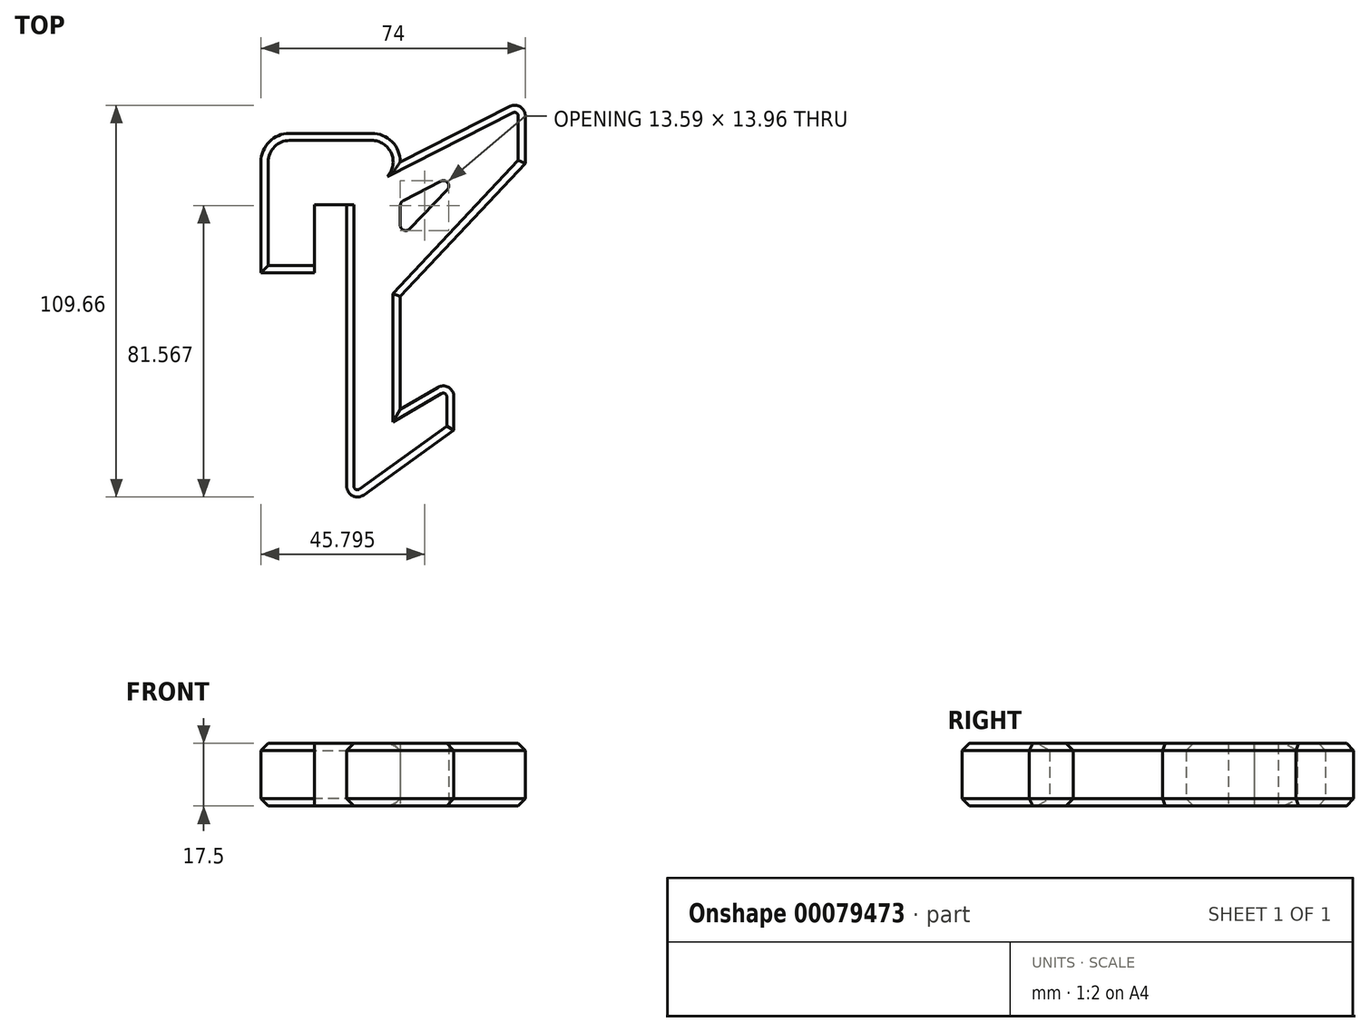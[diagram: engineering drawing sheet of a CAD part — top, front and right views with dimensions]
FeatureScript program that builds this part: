
annotation { "Feature Type Name" : "Feature", "Feature Type Description" : "" }
export const myFeature = defineFeature(function(context is Context, id is Id, definition is map)
    precondition{}
    {
        {
            var Q0;
            Q0=qCreatedBy(makeId("Top.planeOp"),FACE);
            var sketch = newSketch(context, id + "F0", { "sketchPlane" : qUnion([Q0])});
            skLineSegment(sketch, "E0", {"start": v(0, 0) * mm, "end": v(0, -74.06) * mm});
            skLineSegment(sketch, "E1", {"start": v(-9, 0) * mm, "end": v(-9, -19) * mm, "construction": true});
            skLineSegment(sketch, "E2", {"start": v(15, -25.65) * mm, "end": v(50, 11.63) * mm});
            skLineSegment(sketch, "E3", {"start": v(50, 11.63) * mm, "end": v(50, 24.87) * mm});
            skLineSegment(sketch, "E4", {"start": v(45.64, 27.54) * mm, "end": v(15, 12) * mm});
            skLineSegment(sketch, "E5", {"start": v(15, -25.65) * mm, "end": v(15, -57.31) * mm});
            skLineSegment(sketch, "E6", {"start": v(15, -57.31) * mm, "end": v(25.47, -51.12) * mm});
            skLineSegment(sketch, "E7", {"start": v(30, -53.7) * mm, "end": v(30, -63.05) * mm});
            skLineSegment(sketch, "E8", {"start": v(30, -63.05) * mm, "end": v(4.75, -81.23) * mm});
            skLineSegment(sketch, "E9", {"start": v(0, -78.8) * mm, "end": v(0, 0) * mm});
            skLineSegment(sketch, "E10", {"start": v(-9, 0) * mm, "end": v(-9, -19) * mm});
            skPoint(sketch, "E11.visualSharp", {"position": v(50, 29.75) * mm});
            skArc(sketch, "E11.filletArc", {"start": v(50, 24.87) * mm, "mid": v(48.57, 27.43) * mm, "end": v(45.64, 27.54) * mm});
            skPoint(sketch, "E12.visualSharp", {"position": v(30, -48.45) * mm});
            skArc(sketch, "E12.filletArc", {"start": v(30, -53.7) * mm, "mid": v(28.49, -51.1) * mm, "end": v(25.47, -51.12) * mm});
            skPoint(sketch, "E13.visualSharp", {"position": v(0, -84.65) * mm});
            skArc(sketch, "E13.filletArc", {"start": v(0, -78.8) * mm, "mid": v(1.63, -81.46) * mm, "end": v(4.75, -81.23) * mm});
            skLineSegment(sketch, "E14", {"start": v(-24, -19) * mm, "end": v(-24, 12) * mm});
            skLineSegment(sketch, "E15", {"start": v(-16, 20) * mm, "end": v(7, 20) * mm});
            skLineSegment(sketch, "E16", {"start": v(15, 12) * mm, "end": v(15, 12) * mm});
            skPoint(sketch, "E17.visualSharp", {"position": v(15, 20) * mm});
            skArc(sketch, "E17.filletArc", {"start": v(15, 12) * mm, "mid": v(12.66, 17.66) * mm, "end": v(7, 20) * mm});
            skPoint(sketch, "E18.visualSharp", {"position": v(-24, 20) * mm});
            skArc(sketch, "E18.filletArc", {"start": v(-16, 20) * mm, "mid": v(-21.66, 17.66) * mm, "end": v(-24, 12) * mm});
            skLineSegment(sketch, "E19", {"start": v(-24, -19) * mm, "end": v(-9, -19) * mm});
            skLineSegment(sketch, "E20", {"start": v(-9, 0) * mm, "end": v(0, 0) * mm});
            skLineSegment(sketch, "E21", {"start": v(15, -0.24) * mm, "end": v(15, -5.7) * mm});
            skLineSegment(sketch, "E22", {"start": v(17.58, -6.75) * mm, "end": v(28.17, 4.23) * mm});
            skLineSegment(sketch, "E23", {"start": v(26.4, 6.6) * mm, "end": v(15.8, 1.1) * mm});
            skPoint(sketch, "E24.visualSharp", {"position": v(15, 0.67) * mm});
            skArc(sketch, "E24.filletArc", {"start": v(15.8, 1.1) * mm, "mid": v(15.22, 0.54) * mm, "end": v(15, -0.24) * mm});
            skPoint(sketch, "E25.visualSharp", {"position": v(34.55, 10.84) * mm});
            skArc(sketch, "E25.filletArc", {"start": v(28.17, 4.23) * mm, "mid": v(28.3, 6.17) * mm, "end": v(26.4, 6.6) * mm});
            skPoint(sketch, "E26.visualSharp", {"position": v(15, -9.42) * mm});
            skArc(sketch, "E26.filletArc", {"start": v(15, -5.7) * mm, "mid": v(15.94, -7.1) * mm, "end": v(17.58, -6.75) * mm});
            skSolve(sketch);
        }
        {
            var Q0;
            Q0=makeQuery(id+"F0.imprint","IMPRINT",FACE,{"disambiguationData":[TD([[makeQuery(id+"F0.imprint","IMPRINT",EDGE,{"derivedFrom":sQuery(id+"F0.wireOp",EDGE,"E2")}),1.0]])]});
            extrude(context, id + "F1", {"entities" : qUnion([Q0]), "depth" : 17.5 * mm, "offsetDistance" : 25 * mm});
        }
        {
            var Q0;
            Q0=makeQuery(id+"F1.opExtrude","CAP_EDGE",EDGE,{"disambiguationData":[OSD([sQuery(id+"F0.wireOp",EDGE,"E4")])],"isStart":false});
            var Q1;
            Q1=makeQuery(id+"F1.opExtrude","CAP_EDGE",EDGE,{"disambiguationData":[OSD([sQuery(id+"F0.wireOp",EDGE,"E2")])],"isStart":false});
            var Q2;
            Q2=makeQuery(id+"F1.opExtrude","CAP_EDGE",EDGE,{"disambiguationData":[OSD([sQuery(id+"F0.wireOp",EDGE,"E3")])],"isStart":false});
            var Q3;
            Q3=makeQuery(id+"F1.opExtrude","CAP_EDGE",EDGE,{"disambiguationData":[OSD([sQuery(id+"F0.wireOp",EDGE,"E5")])],"isStart":false});
            var Q4;
            Q4=makeQuery(id+"F1.opExtrude","CAP_EDGE",EDGE,{"disambiguationData":[OSD([sQuery(id+"F0.wireOp",EDGE,"E6")])],"isStart":false});
            var Q5;
            Q5=makeQuery(id+"F1.opExtrude","CAP_EDGE",EDGE,{"disambiguationData":[OSD([sQuery(id+"F0.wireOp",EDGE,"E8")])],"isStart":false});
            var Q6;
            Q6=makeQuery(id+"F1.opExtrude","CAP_EDGE",EDGE,{"disambiguationData":[OSD([sQuery(id+"F0.wireOp",EDGE,"E15")])],"isStart":false});
            var Q7;
            Q7=makeQuery(id+"F1.opExtrude","CAP_EDGE",EDGE,{"disambiguationData":[OSD([sQuery(id+"F0.wireOp",EDGE,"E17.filletArc")])],"isStart":false});
            var Q8;
            Q8=makeQuery(id+"F1.opExtrude","CAP_EDGE",EDGE,{"disambiguationData":[OSD([sQuery(id+"F0.wireOp",EDGE,"E19")])],"isStart":false});
            var Q9;
            Q9=makeQuery(id+"F1.opExtrude","CAP_EDGE",EDGE,{"disambiguationData":[OSD([sQuery(id+"F0.wireOp",EDGE,"E9")])],"isStart":false});
            var Q10;
            Q10=makeQuery(id+"F1.opExtrude","CAP_EDGE",EDGE,{"disambiguationData":[OSD([sQuery(id+"F0.wireOp",EDGE,"E7")])],"isStart":true});
            var Q11;
            Q11=makeQuery(id+"F1.opExtrude","CAP_EDGE",EDGE,{"disambiguationData":[OSD([sQuery(id+"F0.wireOp",EDGE,"E12.filletArc")])],"isStart":true});
            var Q12;
            Q12=makeQuery(id+"F1.opExtrude","CAP_EDGE",EDGE,{"disambiguationData":[OSD([sQuery(id+"F0.wireOp",EDGE,"E5")])],"isStart":true});
            var Q13;
            Q13=makeQuery(id+"F1.opExtrude","CAP_EDGE",EDGE,{"disambiguationData":[OSD([sQuery(id+"F0.wireOp",EDGE,"E2")])],"isStart":true});
            var Q14;
            Q14=makeQuery(id+"F1.opExtrude","CAP_EDGE",EDGE,{"disambiguationData":[OSD([sQuery(id+"F0.wireOp",EDGE,"E3")])],"isStart":true});
            var Q15;
            Q15=makeQuery(id+"F1.opExtrude","CAP_EDGE",EDGE,{"disambiguationData":[OSD([sQuery(id+"F0.wireOp",EDGE,"E4")])],"isStart":true});
            var Q16;
            Q16=makeQuery(id+"F1.opExtrude","CAP_EDGE",EDGE,{"disambiguationData":[OSD([sQuery(id+"F0.wireOp",EDGE,"E17.filletArc")])],"isStart":true});
            var Q17;
            Q17=makeQuery(id+"F1.opExtrude","CAP_EDGE",EDGE,{"disambiguationData":[OSD([sQuery(id+"F0.wireOp",EDGE,"E15")])],"isStart":true});
            var Q18;
            Q18=makeQuery(id+"F1.opExtrude","CAP_EDGE",EDGE,{"disambiguationData":[OSD([sQuery(id+"F0.wireOp",EDGE,"E14")])],"isStart":true});
            var Q19;
            Q19=makeQuery(id+"F1.opExtrude","CAP_EDGE",EDGE,{"disambiguationData":[OSD([sQuery(id+"F0.wireOp",EDGE,"E19")])],"isStart":true});
            var Q20;
            Q20=makeQuery(id+"F1.opExtrude","CAP_EDGE",EDGE,{"disambiguationData":[OSD([sQuery(id+"F0.wireOp",EDGE,"E8")])],"isStart":true});
            chamfer(context, id + "F2", {"entities" : qUnion([Q0, Q1, Q2, Q3, Q4, Q5, Q6, Q7, Q8, Q9, Q10, Q11, Q12, Q13, Q14, Q15, Q16, Q17, Q18, Q19, Q20]), "width" : 2 * mm, "tangentPropagation" : true});
        }
    });
